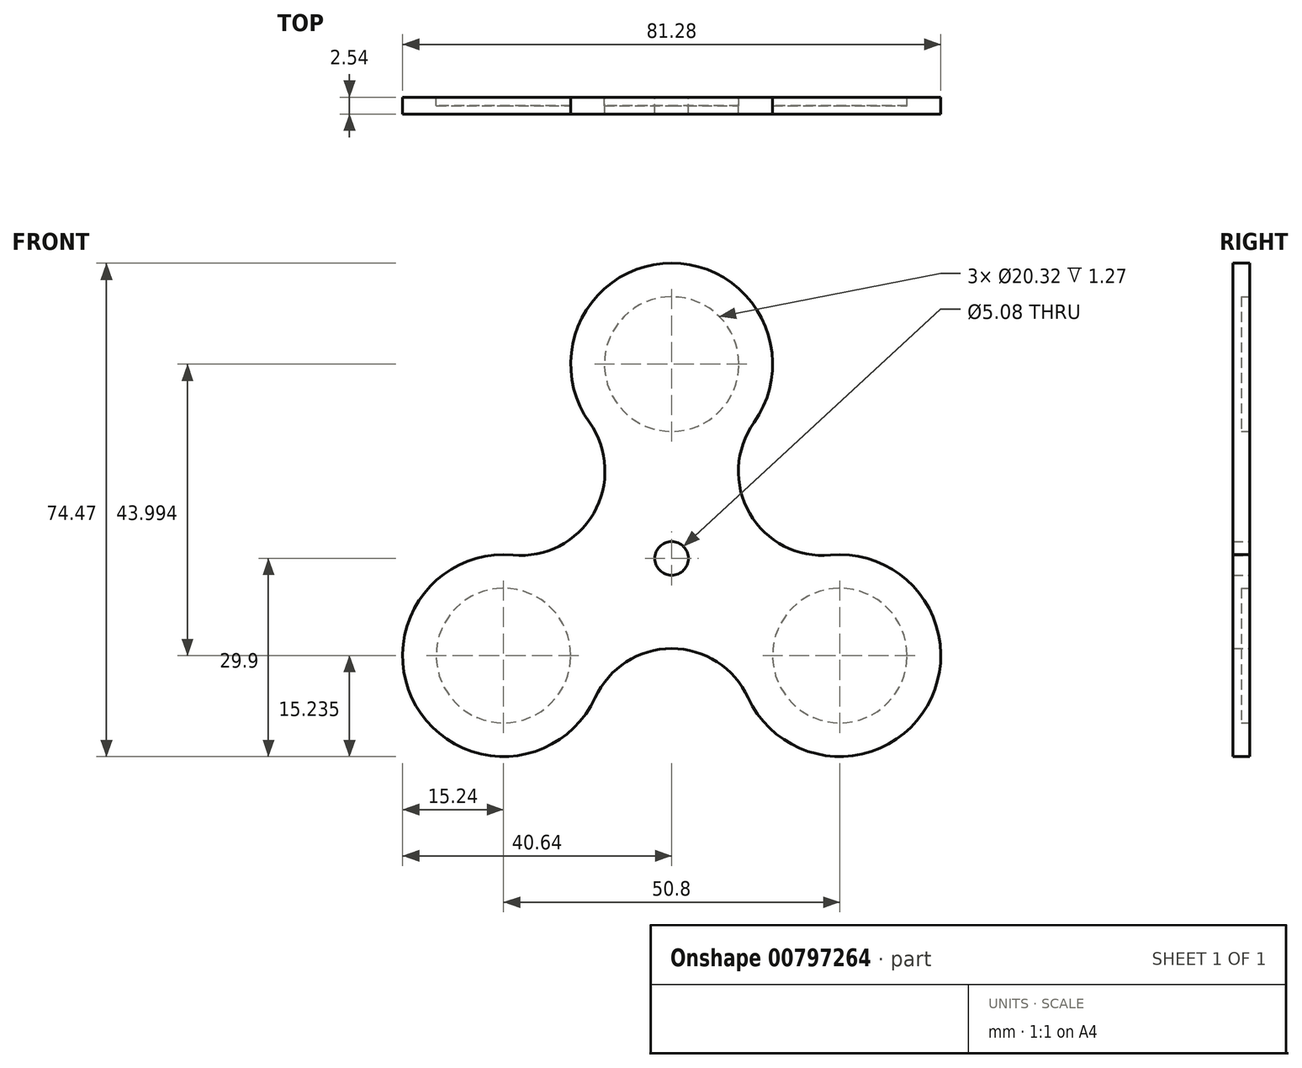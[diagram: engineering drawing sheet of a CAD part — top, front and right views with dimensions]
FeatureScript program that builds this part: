
annotation { "Feature Type Name" : "Feature", "Feature Type Description" : "" }
export const myFeature = defineFeature(function(context is Context, id is Id, definition is map)
    precondition{}
    {
        {
            var Q0;
            Q0=qCreatedBy(makeId("Front.planeOp"),FACE);
            var sketch = newSketch(context, id + "F0", { "sketchPlane" : qUnion([Q0])});
            skLineSegment(sketch, "E0", {"start": v(0, 29.33) * mm, "end": v(-25.4, -14.66) * mm, "construction": true});
            skLineSegment(sketch, "E1", {"start": v(-25.4, -14.66) * mm, "end": v(25.4, -14.66) * mm, "construction": true});
            skLineSegment(sketch, "E2", {"start": v(25.4, -14.66) * mm, "end": v(0, 29.33) * mm, "construction": true});
            skLineSegment(sketch, "E3", {"start": v(25.4, -14.66) * mm, "end": v(-12.7, 7.33) * mm, "construction": true});
            skArc(sketch, "E4", {"start": v(12.43, 20.5) * mm, "mid": v(0, 44.57) * mm, "end": v(-12.43, 20.5) * mm});
            skArc(sketch, "E5", {"start": v(11.55, -21.01) * mm, "mid": v(38.6, -22.28) * mm, "end": v(23.97, 0.5) * mm});
            skArc(sketch, "E6", {"start": v(-23.97, 0.5) * mm, "mid": v(-38.6, -22.28) * mm, "end": v(-11.55, -21.01) * mm});
            skArc(sketch, "E7", {"start": v(-23.97, 0.5) * mm, "mid": v(-11.78, 6.8) * mm, "end": v(-12.43, 20.5) * mm});
            skArc(sketch, "E8", {"start": v(11.55, -21.01) * mm, "mid": v(0, -13.6) * mm, "end": v(-11.55, -21.01) * mm});
            skArc(sketch, "E9", {"start": v(12.43, 20.5) * mm, "mid": v(11.78, 6.8) * mm, "end": v(23.97, 0.5) * mm});
            skCircle(sketch, "E10", {"center": v(0, 29.33) * mm, "radius": 2.54 * mm, "construction": true});
            skCircle(sketch, "E11", {"center": v(25.4, -14.66) * mm, "radius": 2.54 * mm, "construction": true});
            skCircle(sketch, "E12", {"center": v(-25.4, -14.66) * mm, "radius": 2.54 * mm, "construction": true});
            skCircle(sketch, "E13", {"center": v(0, 0) * mm, "radius": 2.54 * mm});
            skSolve(sketch);
        }
        {
            var Q0;
            Q0 = qSketchRegion(id + "F0", true);
            var Q1;
            {var subQ1=sQuery(id+"F0.wireOp",EDGE,"E0");var subQ7=sQuery(id+"F0.wireOp",EDGE,"E3");var subQ8=makeQuery(id+"F0.imprint","INTERSECT",VERTEX,{"derivedFrom":[subQ1,subQ7]});Q1=makeQuery(id+"F0.imprint","IMPRINT",FACE,{"disambiguationData":[TD([[makeQuery(id+"F0.imprint","IMPRINT",EDGE,{"disambiguationData":[TD([[subQ8,1.0]])],"derivedFrom":subQ1}),1.0]])]});}
            var Q2;
            {var subQ1=sQuery(id+"F0.wireOp",EDGE,"E2");var subQ3=sQuery(id+"F0.wireOp",EDGE,"E5");var subQ4=makeQuery(id+"F0.imprint","INTERSECT",VERTEX,{"derivedFrom":[subQ1,subQ3]});Q2=makeQuery(id+"F0.imprint","IMPRINT",FACE,{"disambiguationData":[TD([[makeQuery(id+"F0.imprint","IMPRINT",EDGE,{"disambiguationData":[TD([[subQ4,-1.0]])],"derivedFrom":subQ3}),1.0]])]});}
            var Q3;
            {var subQ1=sQuery(id+"F0.wireOp",EDGE,"E1");var subQ3=sQuery(id+"F0.wireOp",EDGE,"E5");var subQ4=makeQuery(id+"F0.imprint","INTERSECT",VERTEX,{"derivedFrom":[subQ1,subQ3]});Q3=makeQuery(id+"F0.imprint","IMPRINT",FACE,{"disambiguationData":[TD([[makeQuery(id+"F0.imprint","IMPRINT",EDGE,{"disambiguationData":[TD([[subQ4,1.0]])],"derivedFrom":subQ3}),1.0]])]});}
            var Q4;
            {var subQ3=sQuery(id+"F0.wireOp",EDGE,"E3");var subQ5=sQuery(id+"F0.wireOp",EDGE,"E0");var subQ6=makeQuery(id+"F0.imprint","INTERSECT",VERTEX,{"derivedFrom":[subQ5,subQ3]});Q4=makeQuery(id+"F0.imprint","IMPRINT",FACE,{"disambiguationData":[TD([[makeQuery(id+"F0.imprint","IMPRINT",EDGE,{"disambiguationData":[TD([[subQ6,-1.0]])],"derivedFrom":subQ5}),1.0]])]});}
            var Q5;
            {var subQ0=sQuery(id+"F0.wireOp",EDGE,"E1");var subQ1=sQuery(id+"F0.wireOp",EDGE,"E0");var subQ2=makeQuery(id+"F0.imprint","INTERSECT",VERTEX,{"derivedFrom":[subQ1,subQ0]});Q5=makeQuery(id+"F0.imprint","IMPRINT",FACE,{"disambiguationData":[TD([[makeQuery(id+"F0.imprint","IMPRINT",EDGE,{"disambiguationData":[TD([[subQ2,1.0]])],"derivedFrom":subQ1}),1.0]])]});}
            var Q6;
            {var subQ0=sQuery(id+"F0.wireOp",EDGE,"E2");var subQ1=sQuery(id+"F0.wireOp",EDGE,"E0");var subQ2=makeQuery(id+"F0.imprint","INTERSECT",VERTEX,{"derivedFrom":[subQ1,subQ0]});Q6=makeQuery(id+"F0.imprint","IMPRINT",FACE,{"disambiguationData":[TD([[makeQuery(id+"F0.imprint","IMPRINT",EDGE,{"disambiguationData":[TD([[subQ2,-1.0]])],"derivedFrom":subQ1}),1.0]])]});}
            extrude(context, id + "F1", {"entities" : qUnion([Q0, Q1, Q2, Q3, Q4, Q5, Q6]), "depth" : 2.54 * mm, "offsetDistance" : 25.4 * mm});
        }
        {
            var Q0;
            Q0=makeQuery(id+"F1.opExtrude","CAP_FACE",FACE,{"disambiguationData":[OSD([sQuery(id+"F0.wireOp",EDGE,"E4"),sQuery(id+"F0.wireOp",EDGE,"E5"),sQuery(id+"F0.wireOp",EDGE,"E6"),sQuery(id+"F0.wireOp",EDGE,"E7"),sQuery(id+"F0.wireOp",EDGE,"E8"),sQuery(id+"F0.wireOp",EDGE,"E9"),sQuery(id+"F0.wireOp",EDGE,"E13")])],"isStart":true});
            var sketch = newSketch(context, id + "F2", { "sketchPlane" : qUnion([Q0])});
            skCircle(sketch, "E14", {"center": v(25.4, -14.66) * mm, "radius": 10.16 * mm});
            skCircle(sketch, "E15", {"center": v(0, 29.33) * mm, "radius": 10.16 * mm});
            skCircle(sketch, "E16", {"center": v(-25.4, -14.66) * mm, "radius": 10.16 * mm});
            skSolve(sketch);
        }
        {
            var Q0;
            Q0=makeQuery(id+"F2.imprint","IMPRINT",FACE,{"disambiguationData":[TD([[makeQuery(id+"F2.imprint","IMPRINT",EDGE,{"derivedFrom":sQuery(id+"F2.wireOp",EDGE,"E14")}),1.0]])]});
            var Q1;
            Q1=makeQuery(id+"F2.imprint","IMPRINT",FACE,{"disambiguationData":[TD([[makeQuery(id+"F2.imprint","IMPRINT",EDGE,{"derivedFrom":sQuery(id+"F2.wireOp",EDGE,"E15")}),1.0]])]});
            var Q2;
            Q2=makeQuery(id+"F2.imprint","IMPRINT",FACE,{"disambiguationData":[TD([[makeQuery(id+"F2.imprint","IMPRINT",EDGE,{"derivedFrom":sQuery(id+"F2.wireOp",EDGE,"E16")}),1.0]])]});
            extrude(context, id + "F3", {"entities" : qUnion([Q0, Q1, Q2]), "operationType" : NewBodyOperationType.REMOVE, "oppositeDirection" : true, "depth" : 1.27 * mm, "offsetDistance" : 25.4 * mm});
        }
    });
